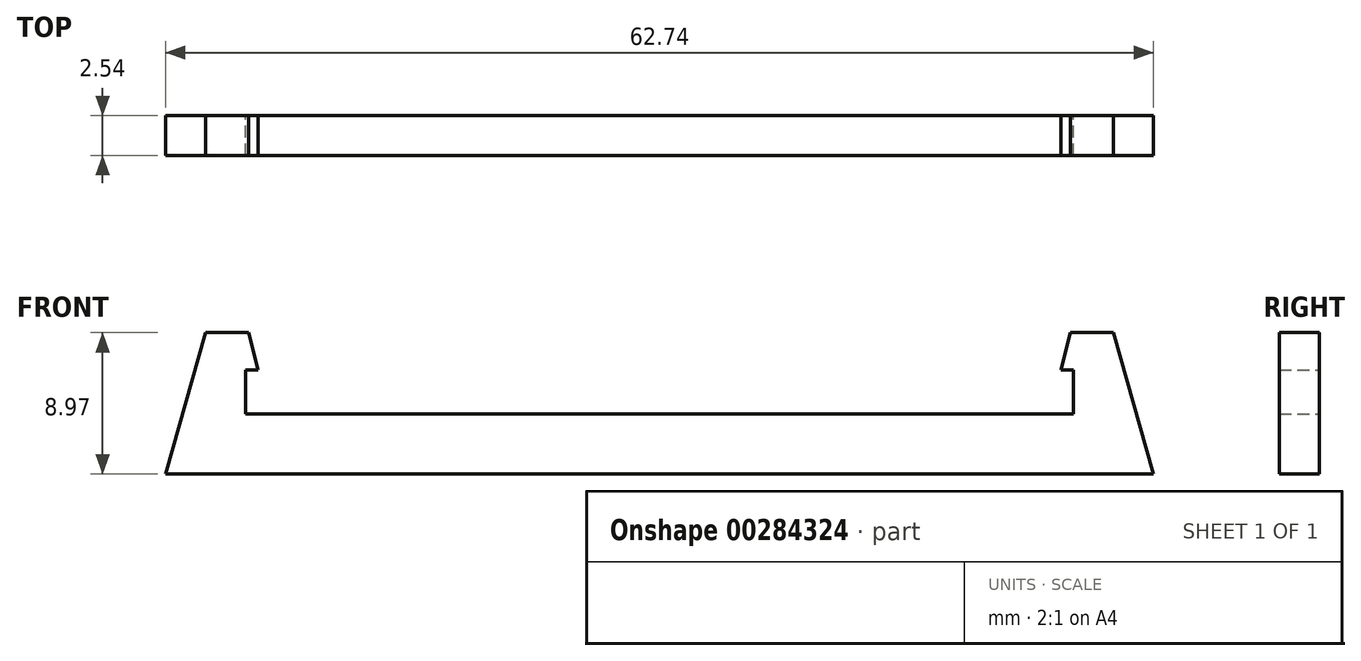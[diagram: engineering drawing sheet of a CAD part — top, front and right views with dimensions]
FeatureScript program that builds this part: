
annotation { "Feature Type Name" : "Feature", "Feature Type Description" : "" }
export const myFeature = defineFeature(function(context is Context, id is Id, definition is map)
    precondition{}
    {
        {
            var Q0;
            Q0=qCreatedBy(makeId("Front.planeOp"),FACE);
            var sketch = newSketch(context, id + "F0", { "sketchPlane" : qUnion([Q0])});
            skLineSegment(sketch, "E0", {"start": v(0, 0) * mm, "end": v(0, 3.8) * mm});
            skLineSegment(sketch, "E1", {"start": v(0, 0) * mm, "end": v(31.37, 0) * mm});
            skLineSegment(sketch, "E2", {"start": v(31.37, 0) * mm, "end": v(28.83, 8.97) * mm});
            skLineSegment(sketch, "E3", {"start": v(28.83, 8.97) * mm, "end": v(26.1, 8.97) * mm});
            skLineSegment(sketch, "E4", {"start": v(26.1, 8.97) * mm, "end": v(25.5, 6.59) * mm});
            skLineSegment(sketch, "E5", {"start": v(25.5, 6.59) * mm, "end": v(26.3, 6.59) * mm});
            skLineSegment(sketch, "E6", {"start": v(26.3, 6.59) * mm, "end": v(26.3, 3.81) * mm});
            skLineSegment(sketch, "E7", {"start": v(26.3, 3.81) * mm, "end": v(0, 3.8) * mm});
            skLineSegment(sketch, "E8", {"start": v(0, 3.8) * mm, "end": v(0, 8.97) * mm, "construction": true});
            skSolve(sketch);
        }
        {
            var Q0;
            Q0=makeQuery(id+"F0.imprint","IMPRINT",FACE,{"disambiguationData":[TD([[makeQuery(id+"F0.imprint","IMPRINT",EDGE,{"derivedFrom":sQuery(id+"F0.wireOp",EDGE,"E0")}),-1.0]])]});
            extrude(context, id + "F1", {"entities" : qUnion([Q0]), "endBound" : BoundingType.SYMMETRIC, "depth" : 2.54 * mm});
        }
        {
            var Q0;
            Q0=makeQuery(id+"F1.opExtrude","SWEPT_BODY",BODY,{"disambiguationData":[OSD([sQuery(id+"F0.wireOp",EDGE,"E0"),sQuery(id+"F0.wireOp",EDGE,"E1"),sQuery(id+"F0.wireOp",EDGE,"E2"),sQuery(id+"F0.wireOp",EDGE,"E3"),sQuery(id+"F0.wireOp",EDGE,"E4"),sQuery(id+"F0.wireOp",EDGE,"E5"),sQuery(id+"F0.wireOp",EDGE,"E6"),sQuery(id+"F0.wireOp",EDGE,"E7")])]});
            var Q1;
            Q1=qCreatedBy(makeId("Right.planeOp"),FACE);
            mirror(context, id + "F2", {"operationType" : NewBodyOperationType.ADD, "entities" : qUnion([Q0]), "mirrorPlane" : qUnion([Q1])});
        }
    });
